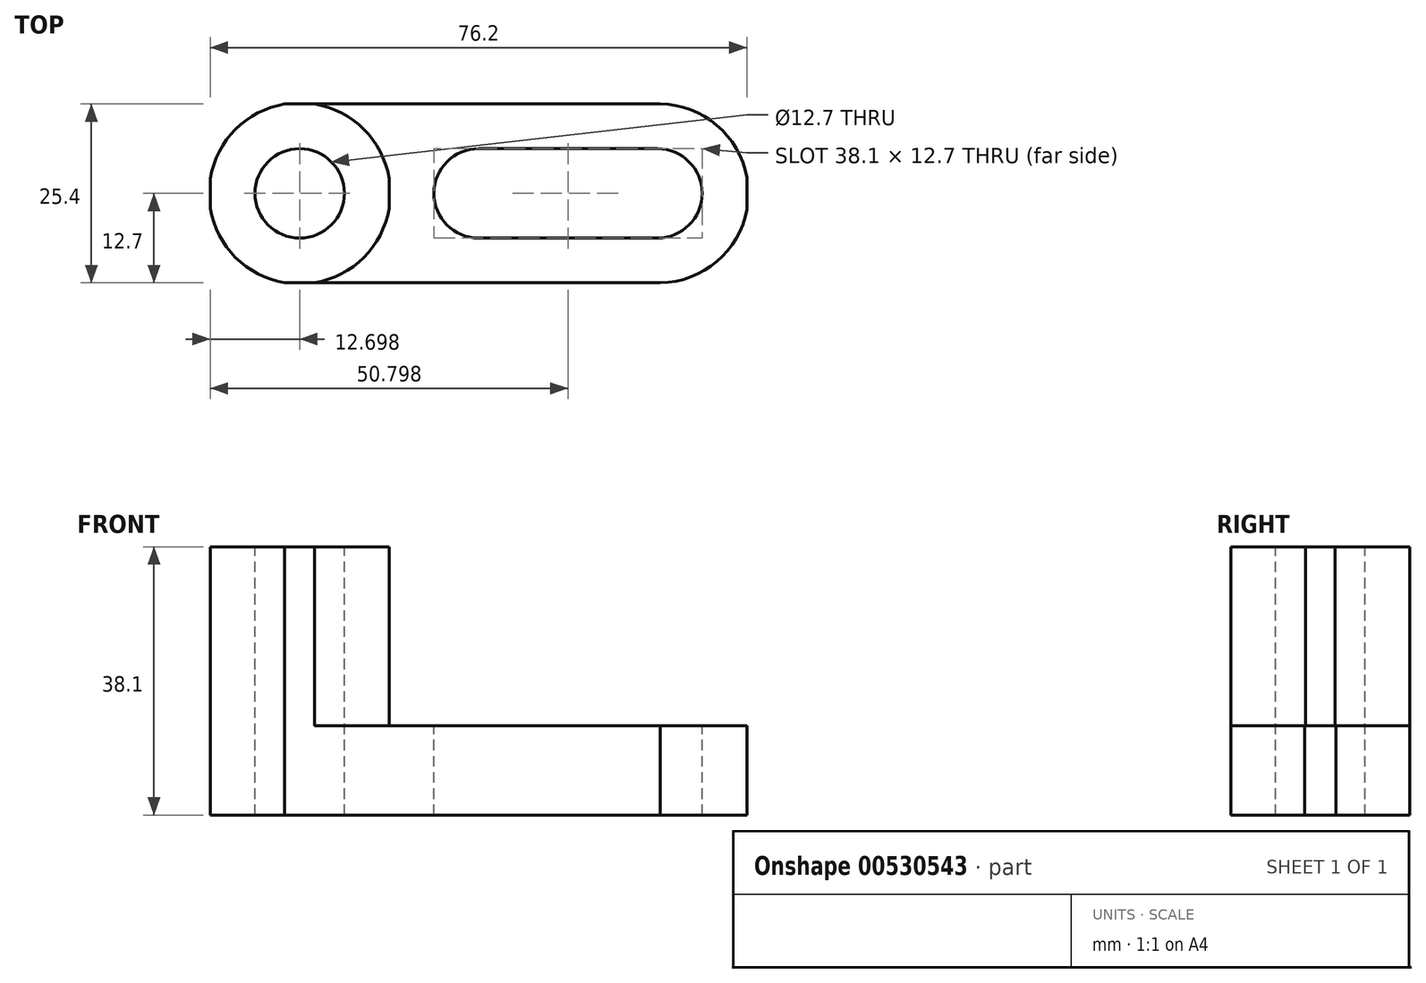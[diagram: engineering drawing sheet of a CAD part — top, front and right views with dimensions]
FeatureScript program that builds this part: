
annotation { "Feature Type Name" : "Feature", "Feature Type Description" : "" }
export const myFeature = defineFeature(function(context is Context, id is Id, definition is map)
    precondition{}
    {
        {
            var Q0;
            Q0=qCreatedBy(makeId("Front.planeOp"),FACE);
            var sketch = newSketch(context, id + "F0", { "sketchPlane" : qUnion([Q0])});
            skLineSegment(sketch, "E0", {"start": v(-44.04, 38.1) * mm, "end": v(-44.04, 0) * mm});
            skLineSegment(sketch, "E1", {"start": v(-44.04, 38.1) * mm, "end": v(-18.64, 38.1) * mm});
            skLineSegment(sketch, "E2", {"start": v(-18.64, 38.1) * mm, "end": v(-18.64, 12.7) * mm});
            skLineSegment(sketch, "E3", {"start": v(-18.64, 12.7) * mm, "end": v(32.16, 12.7) * mm});
            skLineSegment(sketch, "E4", {"start": v(32.16, 12.7) * mm, "end": v(32.16, 0) * mm});
            skLineSegment(sketch, "E5", {"start": v(32.16, 0) * mm, "end": v(-44.04, 0) * mm});
            skSolve(sketch);
        }
        {
            var Q0;
            Q0=makeQuery(id+"F0.imprint","IMPRINT",FACE,{"disambiguationData":[TD([[makeQuery(id+"F0.imprint","IMPRINT",EDGE,{"derivedFrom":sQuery(id+"F0.wireOp",EDGE,"E0")}),1.0]])]});
            extrude(context, id + "F1", {"entities" : qUnion([Q0]), "depth" : 25.4 * mm, "offsetDistance" : 25.4 * mm});
        }
        {
            var Q0;
            Q0=makeQuery(id+"F1.opExtrude","SWEPT_FACE",FACE,{"disambiguationData":[OSD([sQuery(id+"F0.wireOp",EDGE,"E3")])]});
            var sketch = newSketch(context, id + "F2", { "sketchPlane" : qUnion([Q0])});
            skCircle(sketch, "E6", {"center": v(-5.94, -12.7) * mm, "radius": 6.35 * mm});
            skCircle(sketch, "E7", {"center": v(19.46, -12.7) * mm, "radius": 6.35 * mm});
            skLineSegment(sketch, "E8", {"start": v(-5.94, -12.7) * mm, "end": v(-5.94, -19.05) * mm});
            skLineSegment(sketch, "E9", {"start": v(-5.94, -19.05) * mm, "end": v(19.46, -19.05) * mm});
            skLineSegment(sketch, "E10", {"start": v(19.46, -19.05) * mm, "end": v(19.46, -12.7) * mm});
            skLineSegment(sketch, "E11", {"start": v(19.46, -6.35) * mm, "end": v(-5.94, -6.35) * mm});
            skLineSegment(sketch, "E12", {"start": v(-5.94, -6.35) * mm, "end": v(-5.94, -12.7) * mm});
            skSolve(sketch);
        }
        {
            var Q0;
            {var subQ0=sQuery(id+"F2.wireOp",EDGE,"E8");Q0=makeQuery(id+"F2.imprint","IMPRINT",FACE,{"disambiguationData":[TD([[makeQuery(id+"F2.imprint","IMPRINT",EDGE,{"derivedFrom":subQ0}),-1.0]])]});}
            var Q1;
            {var subQ0=sQuery(id+"F2.wireOp",EDGE,"E7");var subQ1=makeQuery(id+"F2.imprint","INTERSECT",VERTEX,{"derivedFrom":[subQ0,sQuery(id+"F2.wireOp",EDGE,"E9")]});Q1=makeQuery(id+"F2.imprint","IMPRINT",FACE,{"disambiguationData":[TD([[makeQuery(id+"F2.imprint","IMPRINT",EDGE,{"disambiguationData":[TD([[subQ1,1.0]])],"derivedFrom":subQ0}),1.0]])]});}
            var Q2;
            {var subQ0=sQuery(id+"F2.wireOp",EDGE,"E9");Q2=makeQuery(id+"F2.imprint","IMPRINT",FACE,{"disambiguationData":[TD([[makeQuery(id+"F2.imprint","IMPRINT",EDGE,{"derivedFrom":subQ0}),1.0]])]});}
            var Q3;
            {var subQ0=sQuery(id+"F2.wireOp",EDGE,"E8");Q3=makeQuery(id+"F2.imprint","IMPRINT",FACE,{"disambiguationData":[TD([[makeQuery(id+"F2.imprint","IMPRINT",EDGE,{"derivedFrom":subQ0}),1.0]])]});}
            extrude(context, id + "F3", {"entities" : qUnion([Q0, Q1, Q2, Q3]), "operationType" : NewBodyOperationType.REMOVE, "endBound" : BoundingType.THROUGH_ALL, "oppositeDirection" : true, "depth" : 25.4 * mm, "offsetDistance" : 25.4 * mm});
        }
        {
            var Q0;
            Q0=makeQuery(id+"F1.opExtrude","SWEPT_FACE",FACE,{"disambiguationData":[OSD([sQuery(id+"F0.wireOp",EDGE,"E3")])]});
            var sketch = newSketch(context, id + "F4", { "sketchPlane" : qUnion([Q0])});
            skArc(sketch, "E13", {"start": v(19.46, -25.4) * mm, "mid": v(32.36, -12.7) * mm, "end": v(19.46, 0) * mm});
            skSolve(sketch);
        }
        {
            var Q0;
            Q0 = qSketchRegion(id + "F4", true);
            var Q1;
            {var subQ0=sQuery(id+"F4.wireOp",EDGE,"E13");var subQ1=sQuery(id+"F0.wireOp",EDGE,"E3");var subQ4=makeQuery(id+"F1.opExtrude","CAP_EDGE",EDGE,{"disambiguationData":[OSD([subQ1])],"isStart":true});var subQ5=makeQuery(id+"F4.imprint","INTERSECT",VERTEX,{"disambiguationData":[OD(1.0)],"derivedFrom":[subQ4,subQ0]});Q1=makeQuery(id+"F4.imprint","IMPRINT",FACE,{"disambiguationData":[TD([[makeQuery(id+"F4.imprint","IMPRINT",EDGE,{"disambiguationData":[TD([[subQ5,1.0]])],"derivedFrom":subQ0}),-1.0]])]});}
            var Q2;
            {var subQ0=sQuery(id+"F4.wireOp",EDGE,"E13");var subQ1=sQuery(id+"F0.wireOp",EDGE,"E3");var subQ2=makeQuery(id+"F1.opExtrude","CAP_EDGE",EDGE,{"disambiguationData":[OSD([subQ1])],"isStart":false});var subQ3=makeQuery(id+"F4.imprint","INTERSECT",VERTEX,{"disambiguationData":[OD(1.0)],"derivedFrom":[subQ2,subQ0]});Q2=makeQuery(id+"F4.imprint","IMPRINT",FACE,{"disambiguationData":[TD([[makeQuery(id+"F4.imprint","IMPRINT",EDGE,{"disambiguationData":[TD([[subQ3,-1.0]])],"derivedFrom":subQ0}),-1.0]])]});}
            extrude(context, id + "F5", {"entities" : qUnion([Q0, Q1, Q2]), "operationType" : NewBodyOperationType.REMOVE, "endBound" : BoundingType.THROUGH_ALL, "oppositeDirection" : true, "depth" : 25.4 * mm, "offsetDistance" : 25.4 * mm});
        }
        {
            var Q0;
            Q0=makeQuery(id+"F1.opExtrude","SWEPT_FACE",FACE,{"disambiguationData":[OSD([sQuery(id+"F0.wireOp",EDGE,"E1")])]});
            var sketch = newSketch(context, id + "F6", { "sketchPlane" : qUnion([Q0])});
            skCircle(sketch, "E14", {"center": v(-31.34, -12.7) * mm, "radius": 12.88 * mm});
            skPoint(sketch, "E14.centerSnap0", {"position": v(-31.34, -25.4) * mm});
            skSolve(sketch);
        }
        {
            var Q0;
            {var subQ0=sQuery(id+"F6.wireOp",EDGE,"E14");var subQ1=sQuery(id+"F0.wireOp",EDGE,"E1");var subQ2=makeQuery(id+"F1.opExtrude","CAP_EDGE",EDGE,{"disambiguationData":[OSD([subQ1])],"isStart":true});var subQ3=makeQuery(id+"F6.imprint","INTERSECT",VERTEX,{"disambiguationData":[OD(0.0)],"derivedFrom":[subQ2,subQ0]});Q0=makeQuery(id+"F6.imprint","IMPRINT",FACE,{"disambiguationData":[TD([[makeQuery(id+"F6.imprint","IMPRINT",EDGE,{"disambiguationData":[TD([[subQ3,1.0]])],"derivedFrom":subQ0}),-1.0]])]});}
            var Q1;
            {var subQ0=sQuery(id+"F6.wireOp",EDGE,"E14");var subQ1=sQuery(id+"F0.wireOp",EDGE,"E1");var subQ2=makeQuery(id+"F1.opExtrude","CAP_EDGE",EDGE,{"disambiguationData":[OSD([subQ1])],"isStart":false});var subQ3=makeQuery(id+"F6.imprint","INTERSECT",VERTEX,{"disambiguationData":[OD(1.0)],"derivedFrom":[subQ2,subQ0]});Q1=makeQuery(id+"F6.imprint","IMPRINT",FACE,{"disambiguationData":[TD([[makeQuery(id+"F6.imprint","IMPRINT",EDGE,{"disambiguationData":[TD([[subQ3,-1.0]])],"derivedFrom":subQ0}),-1.0]])]});}
            var Q2;
            {var subQ0=sQuery(id+"F6.wireOp",EDGE,"E14");var subQ1=sQuery(id+"F0.wireOp",EDGE,"E1");var subQ4=makeQuery(id+"F1.opExtrude","CAP_EDGE",EDGE,{"disambiguationData":[OSD([subQ1])],"isStart":false});var subQ5=makeQuery(id+"F6.imprint","INTERSECT",VERTEX,{"disambiguationData":[OD(0.0)],"derivedFrom":[subQ4,subQ0]});Q2=makeQuery(id+"F6.imprint","IMPRINT",FACE,{"disambiguationData":[TD([[makeQuery(id+"F6.imprint","IMPRINT",EDGE,{"disambiguationData":[TD([[subQ5,1.0]])],"derivedFrom":subQ0}),-1.0]])]});}
            var Q3;
            {var subQ0=sQuery(id+"F6.wireOp",EDGE,"E14");var subQ1=sQuery(id+"F0.wireOp",EDGE,"E1");var subQ2=makeQuery(id+"F1.opExtrude","CAP_EDGE",EDGE,{"disambiguationData":[OSD([subQ1])],"isStart":true});var subQ3=makeQuery(id+"F6.imprint","INTERSECT",VERTEX,{"disambiguationData":[OD(1.0)],"derivedFrom":[subQ2,subQ0]});Q3=makeQuery(id+"F6.imprint","IMPRINT",FACE,{"disambiguationData":[TD([[makeQuery(id+"F6.imprint","IMPRINT",EDGE,{"disambiguationData":[TD([[subQ3,-1.0]])],"derivedFrom":subQ0}),-1.0]])]});}
            extrude(context, id + "F7", {"entities" : qUnion([Q0, Q1, Q2, Q3]), "operationType" : NewBodyOperationType.REMOVE, "oppositeDirection" : true, "depth" : 25.4 * mm, "offsetDistance" : 25.4 * mm});
        }
        {
            var Q0;
            {var subQ0=sQuery(id+"F0.wireOp",EDGE,"E1");var subQ1=makeQuery(id+"F1.opExtrude","CAP_EDGE",EDGE,{"disambiguationData":[OSD([subQ0])],"isStart":false});var subQ2=sQuery(id+"F0.wireOp",EDGE,"E0");var subQ3=makeQuery(id+"F1.opExtrude","SWEPT_EDGE",EDGE,{"disambiguationData":[OSD([subQ2,subQ0])]});var subQ4=makeQuery(id+"F6.imprint","INTERSECT",VERTEX,{"derivedFrom":[subQ3,subQ1]});var subQ5=sQuery(id+"F6.wireOp",EDGE,"E14");var subQ6=makeQuery(id+"F6.imprint","INTERSECT",VERTEX,{"disambiguationData":[OD(0.0)],"derivedFrom":[subQ1,subQ5]});Q0=makeQuery(id+"F7.boolean.opBoolean","COPY",FACE,{"derivedFrom":makeQuery(id+"F7.opExtrude","CAP_FACE",FACE,{"disambiguationData":[OSD([subQ2,subQ0,subQ5]),TDD([makeQuery(id+"F6.imprint","IMPRINT",EDGE,{"disambiguationData":[TD([[subQ6,1.0]])],"derivedFrom":subQ5}),makeQuery(id+"F6.imprint","IMPRINT",EDGE,{"disambiguationData":[TD([[subQ4,-1.0]])],"derivedFrom":subQ3}),makeQuery(id+"F6.imprint","IMPRINT",EDGE,{"disambiguationData":[TD([[subQ6,1.0]])],"derivedFrom":subQ1})])],"isStart":false})});}
            extrude(context, id + "F8", {"entities" : qUnion([Q0]), "operationType" : NewBodyOperationType.REMOVE, "endBound" : BoundingType.THROUGH_ALL, "oppositeDirection" : true, "depth" : 25.4 * mm, "offsetDistance" : 25.4 * mm});
        }
        {
            var Q0;
            {var subQ0=sQuery(id+"F0.wireOp",EDGE,"E1");var subQ1=makeQuery(id+"F1.opExtrude","CAP_EDGE",EDGE,{"disambiguationData":[OSD([subQ0])],"isStart":true});var subQ2=sQuery(id+"F0.wireOp",EDGE,"E0");var subQ3=makeQuery(id+"F1.opExtrude","SWEPT_EDGE",EDGE,{"disambiguationData":[OSD([subQ2,subQ0])]});var subQ4=makeQuery(id+"F6.imprint","INTERSECT",VERTEX,{"derivedFrom":[subQ3,subQ1]});var subQ5=sQuery(id+"F6.wireOp",EDGE,"E14");var subQ6=makeQuery(id+"F6.imprint","INTERSECT",VERTEX,{"disambiguationData":[OD(1.0)],"derivedFrom":[subQ1,subQ5]});Q0=makeQuery(id+"F7.boolean.opBoolean","COPY",FACE,{"derivedFrom":makeQuery(id+"F7.opExtrude","CAP_FACE",FACE,{"disambiguationData":[OSD([subQ2,subQ0,subQ5]),TDD([makeQuery(id+"F6.imprint","IMPRINT",EDGE,{"disambiguationData":[TD([[subQ6,-1.0]])],"derivedFrom":subQ5}),makeQuery(id+"F6.imprint","IMPRINT",EDGE,{"disambiguationData":[TD([[subQ4,1.0]])],"derivedFrom":subQ3}),makeQuery(id+"F6.imprint","IMPRINT",EDGE,{"disambiguationData":[TD([[subQ6,1.0]])],"derivedFrom":subQ1})])],"isStart":false})});}
            extrude(context, id + "F9", {"entities" : qUnion([Q0]), "operationType" : NewBodyOperationType.REMOVE, "endBound" : BoundingType.THROUGH_ALL, "oppositeDirection" : true, "depth" : 25.4 * mm, "offsetDistance" : 25.4 * mm});
        }
        {
            var Q0;
            Q0=makeQuery(id+"F1.opExtrude","SWEPT_FACE",FACE,{"disambiguationData":[OSD([sQuery(id+"F0.wireOp",EDGE,"E1")])]});
            var sketch = newSketch(context, id + "F10", { "sketchPlane" : qUnion([Q0])});
            skCircle(sketch, "E15", {"center": v(-31.34, -12.7) * mm, "radius": 6.35 * mm});
            skSolve(sketch);
        }
        {
            var Q0;
            Q0=makeQuery(id+"F10.imprint","IMPRINT",FACE,{"disambiguationData":[TD([[makeQuery(id+"F10.imprint","IMPRINT",EDGE,{"derivedFrom":sQuery(id+"F10.wireOp",EDGE,"E15")}),1.0]])]});
            extrude(context, id + "F11", {"entities" : qUnion([Q0]), "operationType" : NewBodyOperationType.REMOVE, "endBound" : BoundingType.THROUGH_ALL, "oppositeDirection" : true, "depth" : 25.4 * mm, "offsetDistance" : 25.4 * mm});
        }
    });
